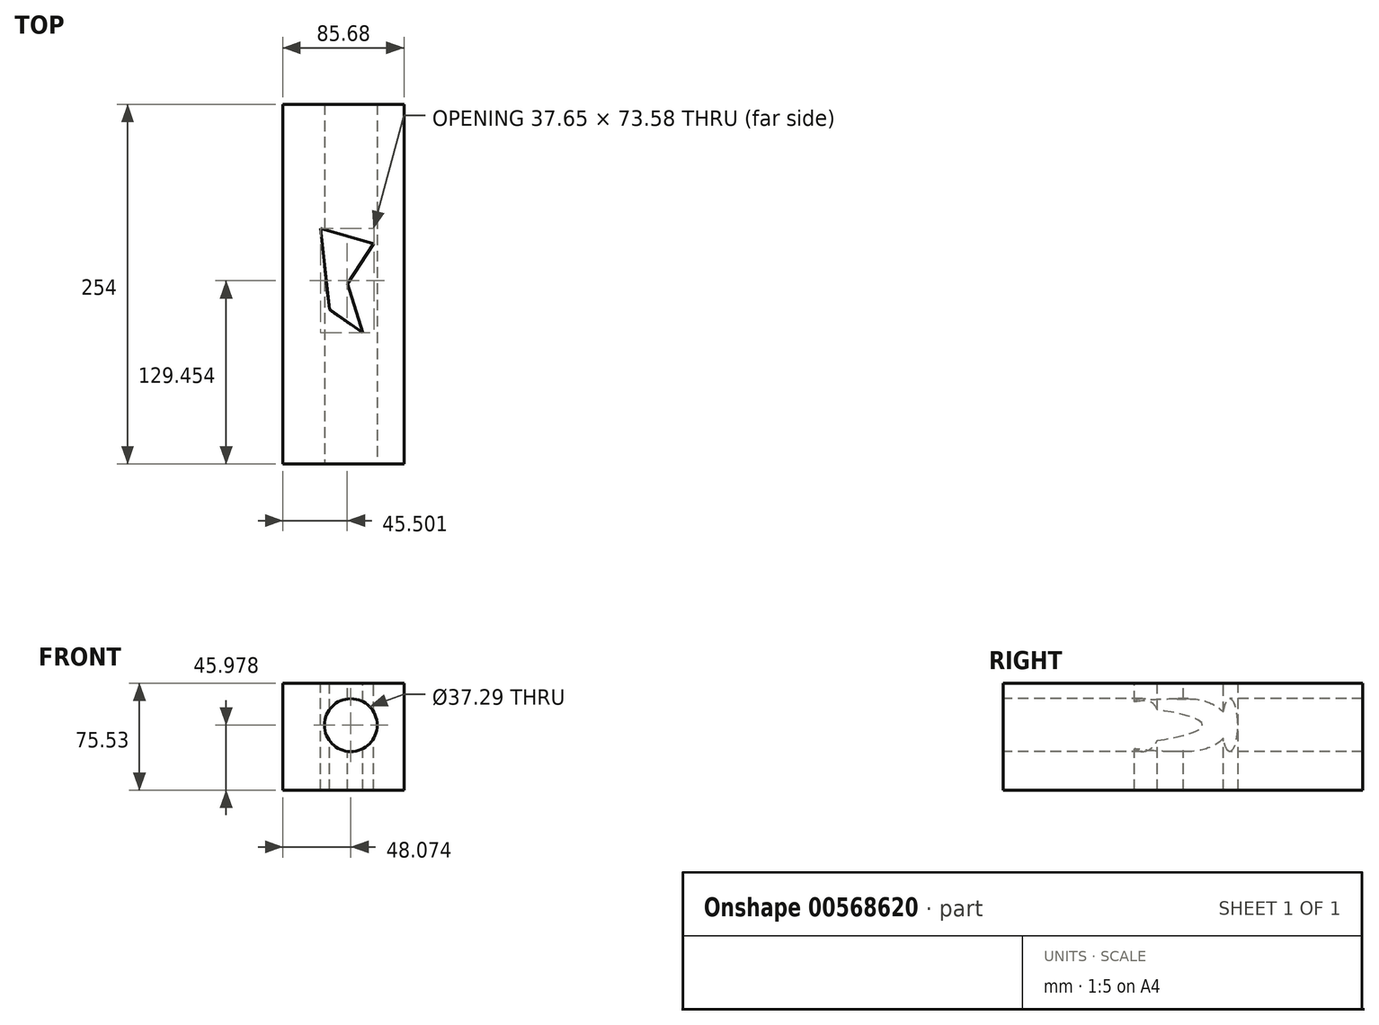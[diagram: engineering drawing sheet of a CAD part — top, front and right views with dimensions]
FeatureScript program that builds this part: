
annotation { "Feature Type Name" : "Feature", "Feature Type Description" : "" }
export const myFeature = defineFeature(function(context is Context, id is Id, definition is map)
    precondition{}
    {
        {
            var Q0;
            Q0=qCreatedBy(makeId("Front.planeOp"),FACE);
            var sketch = newSketch(context, id + "F0", { "sketchPlane" : qUnion([Q0])});
            skLineSegment(sketch, "E0.bottom", {"start": v(0, 0) * mm, "end": v(85.68, 0) * mm});
            skLineSegment(sketch, "E0.top", {"start": v(0, 75.53) * mm, "end": v(85.68, 75.53) * mm});
            skLineSegment(sketch, "E0.left", {"start": v(0, 0) * mm, "end": v(0, 75.53) * mm});
            skLineSegment(sketch, "E0.right", {"start": v(85.68, 0) * mm, "end": v(85.68, 75.53) * mm});
            skSolve(sketch);
        }
        {
            var Q0;
            Q0 = qSketchRegion(id + "F0", true);
            extrude(context, id + "F1", {"entities" : qUnion([Q0]), "depth" : 254 * mm, "offsetDistance" : 25.4 * mm});
        }
        {
            var Q0;
            Q0=makeQuery(id+"F1.opExtrude","CAP_FACE",FACE,{"disambiguationData":[OSD([sQuery(id+"F0.wireOp",EDGE,"E0.bottom"),sQuery(id+"F0.wireOp",EDGE,"E0.top"),sQuery(id+"F0.wireOp",EDGE,"E0.left"),sQuery(id+"F0.wireOp",EDGE,"E0.right")])],"isStart":false});
            var sketch = newSketch(context, id + "F2", { "sketchPlane" : qUnion([Q0])});
            skCircle(sketch, "E1", {"center": v(48.07, 45.98) * mm, "radius": 18.65 * mm});
            skSolve(sketch);
        }
        {
            var Q0;
            Q0=makeQuery(id+"F2.imprint","IMPRINT",FACE,{"disambiguationData":[TD([[makeQuery(id+"F2.imprint","IMPRINT",EDGE,{"derivedFrom":sQuery(id+"F2.wireOp",EDGE,"E1")}),1.0]])]});
            extrude(context, id + "F3", {"entities" : qUnion([Q0]), "operationType" : NewBodyOperationType.REMOVE, "endBound" : BoundingType.THROUGH_ALL, "oppositeDirection" : true, "depth" : 254 * mm, "offsetDistance" : 25.4 * mm});
        }
        {
            var Q0;
            Q0=makeQuery(id+"F1.opExtrude","SWEPT_FACE",FACE,{"disambiguationData":[OSD([sQuery(id+"F0.wireOp",EDGE,"E0.top")])]});
            var sketch = newSketch(context, id + "F4", { "sketchPlane" : qUnion([Q0])});
            skLineSegment(sketch, "E2", {"start": v(26.68, -87.76) * mm, "end": v(64.33, -98.35) * mm});
            skLineSegment(sketch, "E3", {"start": v(64.33, -98.35) * mm, "end": v(45.67, -126.65) * mm});
            skLineSegment(sketch, "E4", {"start": v(45.67, -126.65) * mm, "end": v(56.48, -161.33) * mm});
            skLineSegment(sketch, "E5", {"start": v(56.48, -161.33) * mm, "end": v(32.91, -144.93) * mm});
            skLineSegment(sketch, "E6", {"start": v(32.91, -144.93) * mm, "end": v(26.68, -87.76) * mm});
            skSolve(sketch);
        }
        {
            var Q0;
            Q0=makeQuery(id+"F4.imprint","IMPRINT",FACE,{"disambiguationData":[TD([[makeQuery(id+"F4.imprint","IMPRINT",EDGE,{"derivedFrom":sQuery(id+"F4.wireOp",EDGE,"E2")}),-1.0]])]});
            extrude(context, id + "F5", {"entities" : qUnion([Q0]), "operationType" : NewBodyOperationType.REMOVE, "oppositeDirection" : true, "depth" : 127 * mm, "offsetDistance" : 25.4 * mm});
        }
    });
